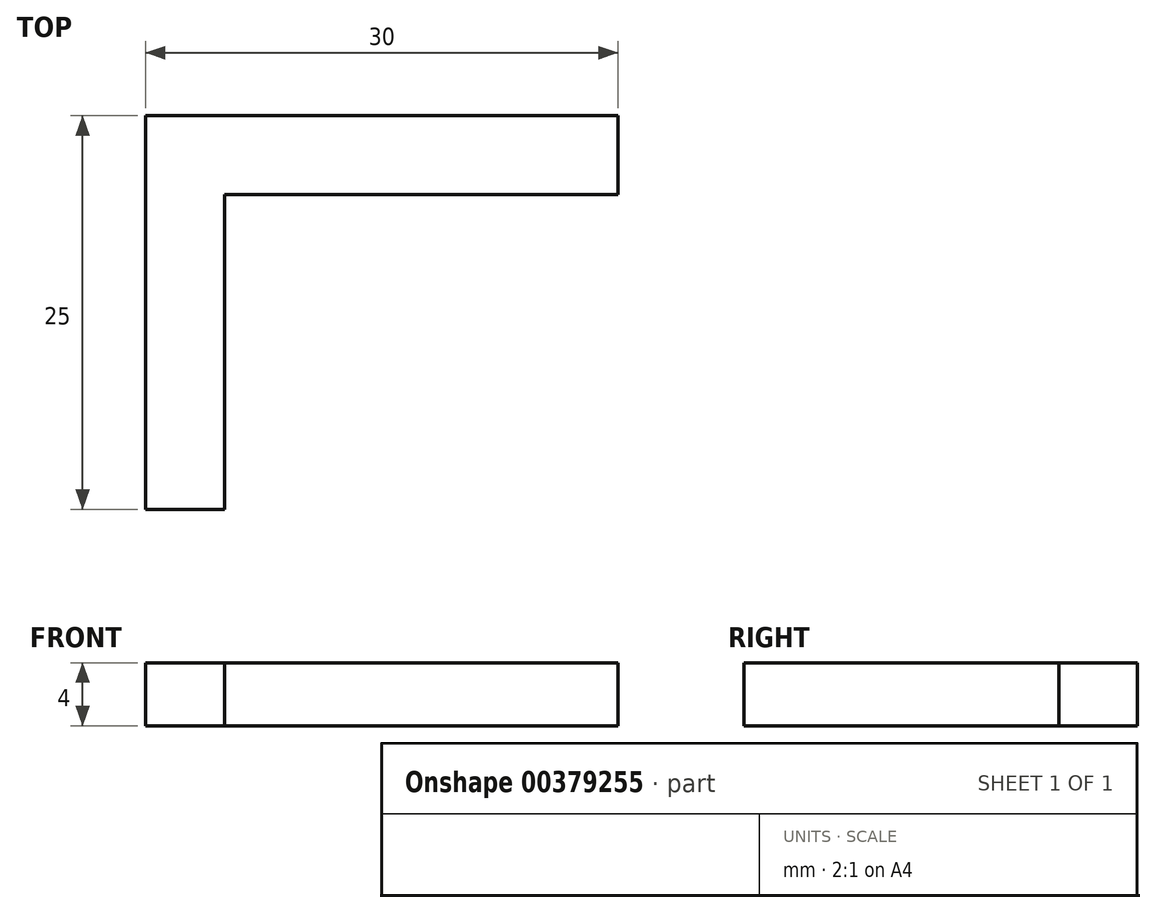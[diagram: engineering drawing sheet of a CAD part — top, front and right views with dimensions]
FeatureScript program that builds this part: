
annotation { "Feature Type Name" : "Feature", "Feature Type Description" : "" }
export const myFeature = defineFeature(function(context is Context, id is Id, definition is map)
    precondition{}
    {
        {
            var Q0;
            Q0=qCreatedBy(makeId("Top.planeOp"),FACE);
            var sketch = newSketch(context, id + "F0", { "sketchPlane" : qUnion([Q0])});
            skLineSegment(sketch, "E0", {"start": v(-5, 0) * mm, "end": v(-5, 25) * mm});
            skLineSegment(sketch, "E1", {"start": v(-5, 25) * mm, "end": v(25, 25) * mm});
            skLineSegment(sketch, "E2", {"start": v(25, 25) * mm, "end": v(25, 20) * mm});
            skLineSegment(sketch, "E3", {"start": v(25, 20) * mm, "end": v(0, 20) * mm});
            skLineSegment(sketch, "E4", {"start": v(0, 20) * mm, "end": v(0, 0) * mm});
            skLineSegment(sketch, "E5", {"start": v(0, 0) * mm, "end": v(-5, 0) * mm});
            skSolve(sketch);
        }
        {
            var Q0;
            Q0=qSketchRegion(id+"F0",true);
            extrude(context, id + "F1", {"entities" : qUnion([Q0]), "depth" : 4 * mm});
        }
    });
